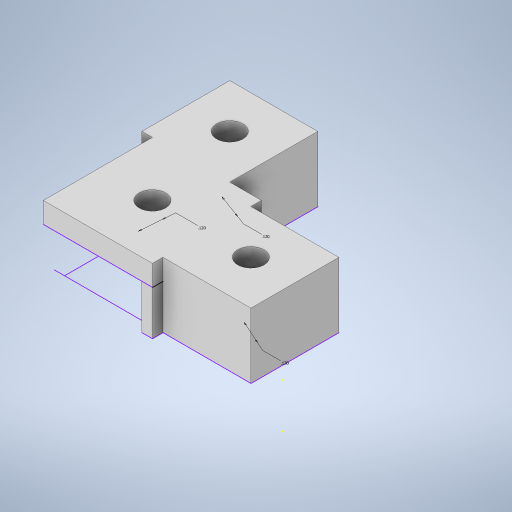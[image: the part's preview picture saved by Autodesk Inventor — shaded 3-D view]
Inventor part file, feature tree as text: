
AUTODESK INVENTOR PART (.ipt)
format: ipt  version: 2024 (Build 280153000, 153)  size: 266,240 bytes
history: native  units: in
note: dims shown in document units (in); Inventor stores cm internally (conversion verified against a paired STEP export)
features: extrude x4, hole x3, sketch x2
ambient origin geometry x8: Origin, YZ Plane, XZ Plane, XY Plane, X Axis, Y Axis, Z Axis, Center Point
bodies: Solid1 (feature_tree)
feature tree (9):
  sketch  "Sketch1"  dims[d0=0.202in d1=0.0in d2=0.094in d3=0.0in]
  extrude  "Extrusion1"  Depth=0.094in TaperAngle=0.0deg
  sketch  "Sketch2"  dims[d4=0.12in d5=0.12in d6=0.75in d7=0.375in d8=0.25in d9=0.5635in d10=1.0in d11=0.8108in d12=0.296in d13=0.0in d14=0.296in d15=0.0in d16=0.12in d17=0.12in d18=0.12in d19=0.75in d20=0.375in d21=0.25in d22=0.5635in d23=1.0in d24=0.8108in d25=0.12in d26=0.75in d27=0.375in d28=0.25in d29=0.5635in d30=1.0in d31=0.8108in]
  extrude  "Extrusion2"  Depth=0.296in TaperAngle=0.0deg
  hole  "Hole1"  [1 undecoded]
  extrude  "Extrusion3"  Depth=0.296in
  extrude  "Extrusion4"  Depth=0.296in
  hole  "Hole2"  [1 undecoded]
  hole  "Hole3"  [1 undecoded]
note: 3 required parameter values undecoded (feature->parameter linkage not recoverable at this tier; creation-order binding heuristic only, values carry confidence <= 0.55)
